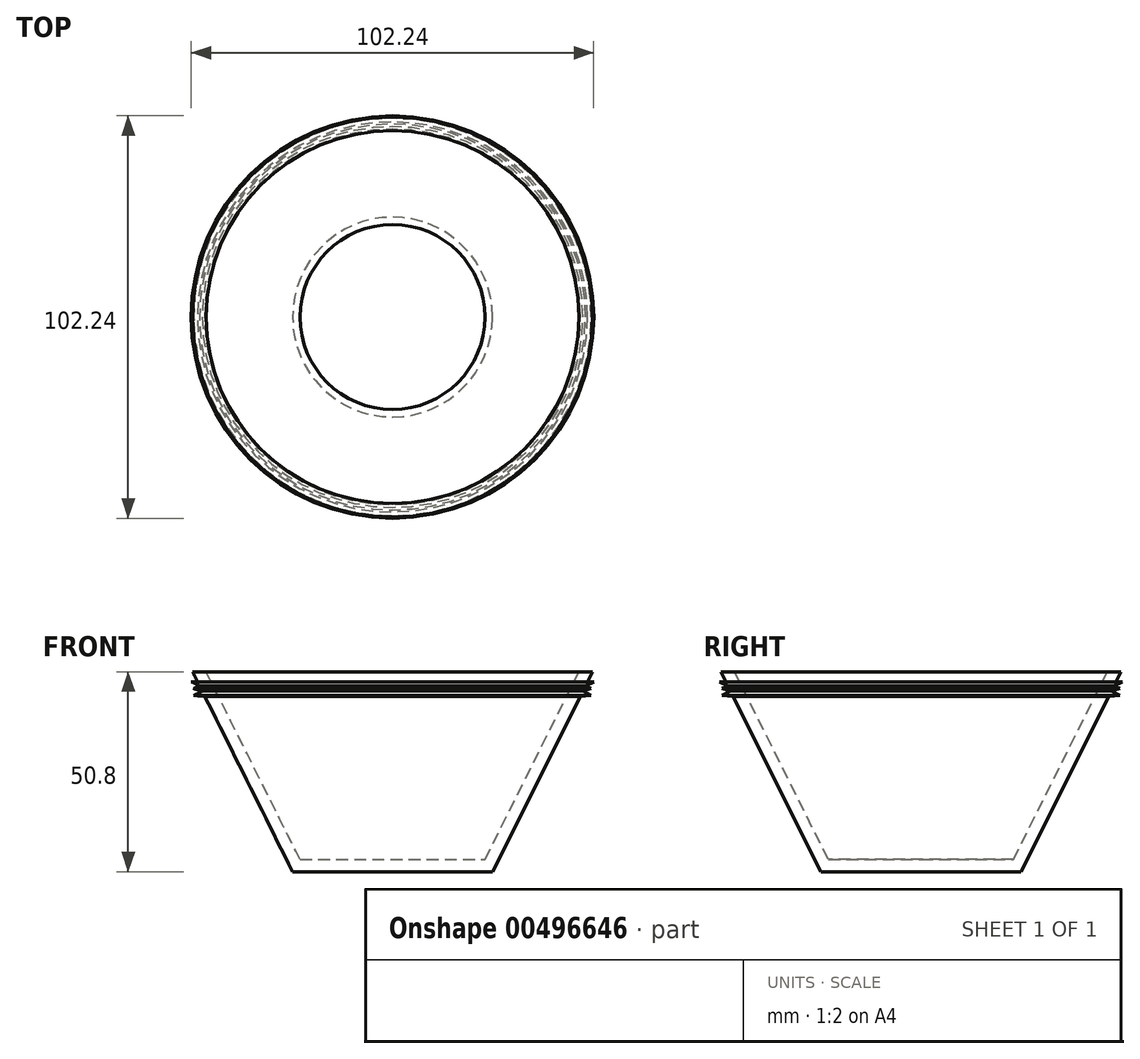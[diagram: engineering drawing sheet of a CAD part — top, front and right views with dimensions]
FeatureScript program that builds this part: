
annotation { "Feature Type Name" : "Feature", "Feature Type Description" : "" }
export const myFeature = defineFeature(function(context is Context, id is Id, definition is map)
    precondition{}
    {
        {
            var Q0;
            Q0=qCreatedBy(makeId("Front.planeOp"),FACE);
            var sketch = newSketch(context, id + "F0", { "sketchPlane" : qUnion([Q0])});
            skLineSegment(sketch, "E0", {"start": v(0, 0) * mm, "end": v(0, 50.8) * mm, "construction": true});
            skLineSegment(sketch, "E1", {"start": v(0, 0) * mm, "end": v(25.4, 0) * mm});
            skLineSegment(sketch, "E2", {"start": v(25.4, 0) * mm, "end": v(50.8, 50.8) * mm});
            skLineSegment(sketch, "E3.0", {"start": v(23.5, 3.07) * mm, "end": v(47.36, 50.8) * mm});
            skLineSegment(sketch, "E3.1", {"start": v(0, 3.07) * mm, "end": v(23.5, 3.07) * mm});
            skLineSegment(sketch, "E4", {"start": v(0, 3.07) * mm, "end": v(0, 0) * mm});
            skLineSegment(sketch, "E5", {"start": v(47.36, 50.8) * mm, "end": v(50.8, 50.8) * mm});
            skLineSegment(sketch, "E6", {"start": v(49.53, 48.26) * mm, "end": v(51.12, 48.26) * mm});
            skLineSegment(sketch, "E7", {"start": v(51.12, 48.26) * mm, "end": v(49.02, 47.24) * mm});
            skLineSegment(sketch, "E8", {"start": v(49.02, 47.24) * mm, "end": v(50.48, 46.5) * mm});
            skLineSegment(sketch, "E9", {"start": v(50.48, 46.5) * mm, "end": v(48.33, 45.86) * mm});
            skLineSegment(sketch, "E10", {"start": v(48.33, 45.86) * mm, "end": v(50.48, 44.78) * mm});
            skLineSegment(sketch, "E11", {"start": v(50.48, 44.78) * mm, "end": v(47.7, 44.58) * mm});
            skSolve(sketch);
        }
        {
            var Q0;
            Q0 = qSketchRegion(id + "F0", true);
            var Q1;
            Q1=sQuery(id+"F0.wireOp",EDGE,"E0");
            revolve(context, id + "F1", {"entities" : qUnion([Q0]), "axis" : qUnion([Q1]), "revolveType" : RevolveType.FULL});
        }
    });
